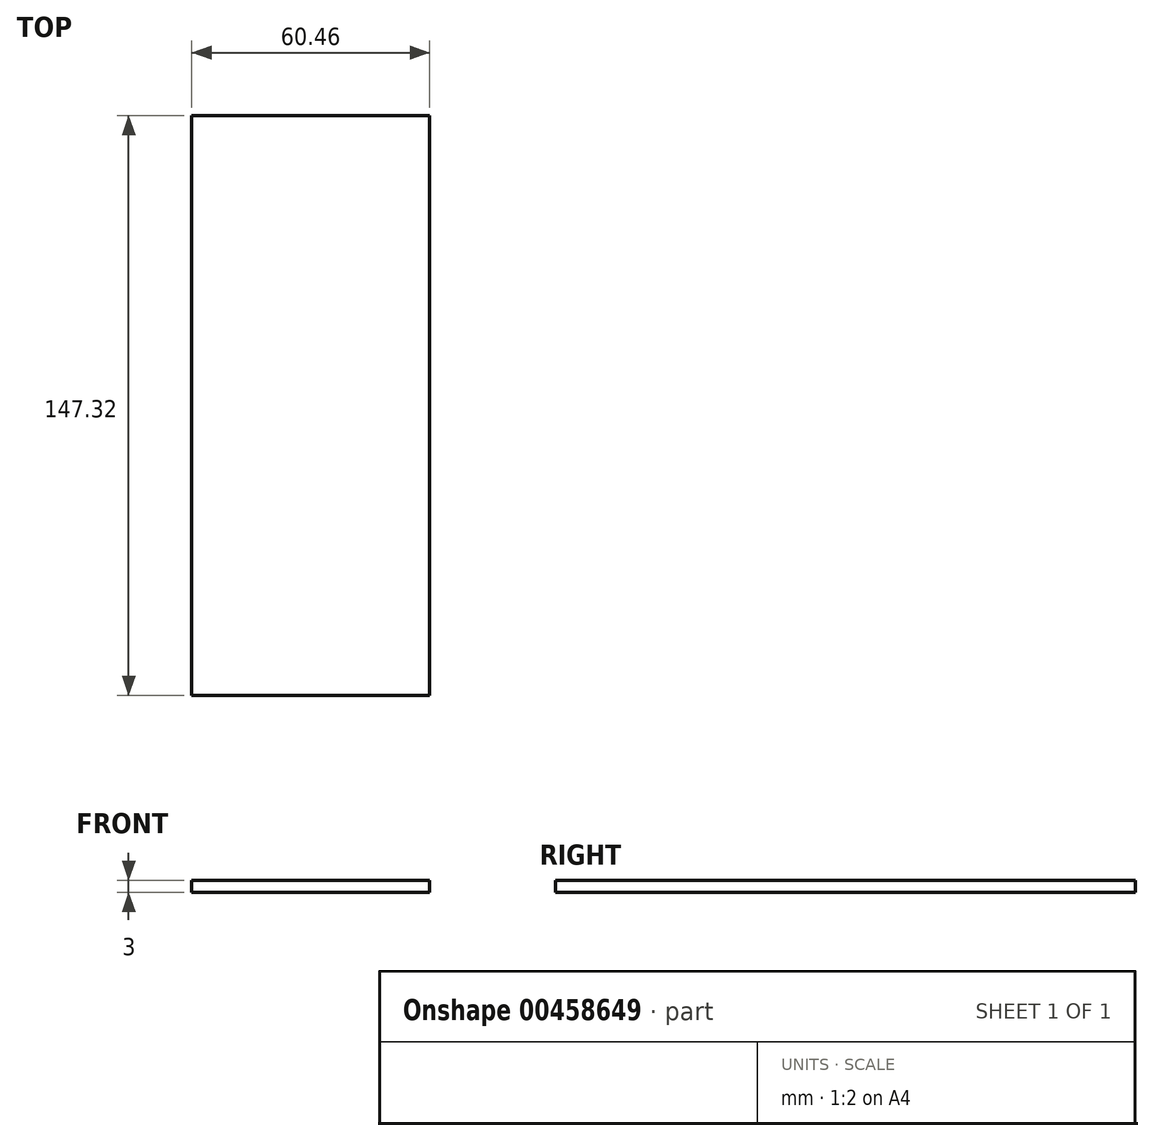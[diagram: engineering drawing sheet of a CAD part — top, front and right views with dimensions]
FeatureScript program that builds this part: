
annotation { "Feature Type Name" : "Feature", "Feature Type Description" : "" }
export const myFeature = defineFeature(function(context is Context, id is Id, definition is map)
    precondition{}
    {
        {
            var Q0;
            Q0=qCreatedBy(makeId("Top.planeOp"),FACE);
            var sketch = newSketch(context, id + "F0", { "sketchPlane" : qUnion([Q0])});
            skLineSegment(sketch, "E0.bottom", {"start": v(-30.23, 73.66) * mm, "end": v(30.23, 73.66) * mm});
            skLineSegment(sketch, "E0.top", {"start": v(-30.23, -73.66) * mm, "end": v(30.23, -73.66) * mm});
            skLineSegment(sketch, "E0.left", {"start": v(-30.23, 73.66) * mm, "end": v(-30.23, -73.66) * mm});
            skLineSegment(sketch, "E0.right", {"start": v(30.23, 73.66) * mm, "end": v(30.23, -73.66) * mm});
            skLineSegment(sketch, "E1", {"start": v(-30.23, 73.66) * mm, "end": v(30.23, -73.66) * mm});
            skSolve(sketch);
        }
        {
            var Q0;
            Q0 = qSketchRegion(id + "F0", true);
            extrude(context, id + "F1", {"entities" : qUnion([Q0]), "depth" : 3 * mm});
        }
    });
